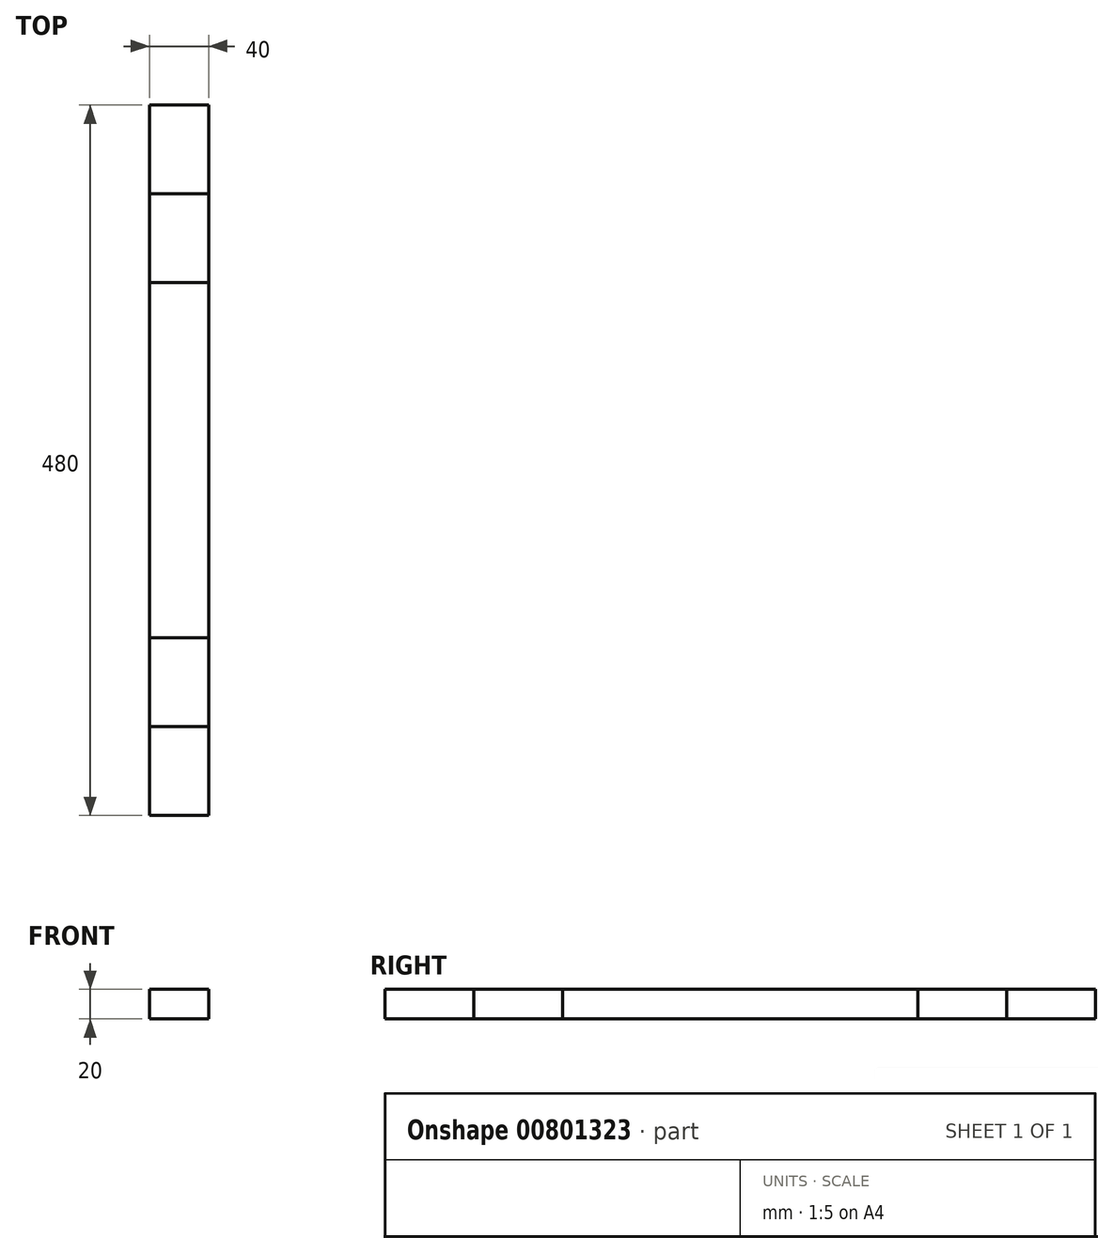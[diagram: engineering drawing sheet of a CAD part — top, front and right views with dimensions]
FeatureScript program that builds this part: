
annotation { "Feature Type Name" : "Feature", "Feature Type Description" : "" }
export const myFeature = defineFeature(function(context is Context, id is Id, definition is map)
    precondition{}
    {
        {
            var Q0;
            Q0=qCreatedBy(makeId("Front.planeOp"),FACE);
            var sketch = newSketch(context, id + "F0", { "sketchPlane" : qUnion([Q0])});
            skLineSegment(sketch, "E0.bottom", {"start": v(20, -10) * mm, "end": v(-20, -10) * mm});
            skLineSegment(sketch, "E0.top", {"start": v(20, 10) * mm, "end": v(-20, 10) * mm});
            skLineSegment(sketch, "E0.left", {"start": v(20, -10) * mm, "end": v(20, 10) * mm});
            skLineSegment(sketch, "E0.right", {"start": v(-20, -10) * mm, "end": v(-20, 10) * mm});
            skPoint(sketch, "E0.middle", {"position": v(0, 0) * mm});
            skSolve(sketch);
        }
        {
            var Q0;
            Q0 = qSketchRegion(id + "F0", true);
            extrude(context, id + "F1", {"entities" : qUnion([Q0]), "endBound" : BoundingType.SYMMETRIC, "depth" : 480 * mm, "offsetDistance" : 25 * mm});
        }
        {
            var Q0;
            Q0=qCreatedBy(makeId("Front.planeOp"),FACE);
            var sketch = newSketch(context, id + "F2", { "sketchPlane" : qUnion([Q0])});
            skLineSegment(sketch, "E1.bottom", {"start": v(20, -10) * mm, "end": v(-20, -10) * mm});
            skLineSegment(sketch, "E1.top", {"start": v(20, 10) * mm, "end": v(-20, 10) * mm});
            skLineSegment(sketch, "E1.left", {"start": v(20, -10) * mm, "end": v(20, 10) * mm});
            skLineSegment(sketch, "E1.right", {"start": v(-20, -10) * mm, "end": v(-20, 10) * mm});
            skPoint(sketch, "E1.middle", {"position": v(0, 0) * mm});
            skSolve(sketch);
        }
        {
            var Q0;
            Q0 = qSketchRegion(id + "F2", true);
            extrude(context, id + "F3", {"entities" : qUnion([Q0]), "endBound" : BoundingType.SYMMETRIC, "depth" : 360 * mm, "offsetDistance" : 25 * mm});
        }
        {
            var Q0;
            Q0=qCreatedBy(makeId("Front.planeOp"),FACE);
            var sketch = newSketch(context, id + "F4", { "sketchPlane" : qUnion([Q0])});
            skLineSegment(sketch, "E2.bottom", {"start": v(20, -10) * mm, "end": v(-20, -10) * mm});
            skLineSegment(sketch, "E2.top", {"start": v(20, 10) * mm, "end": v(-20, 10) * mm});
            skLineSegment(sketch, "E2.left", {"start": v(20, -10) * mm, "end": v(20, 10) * mm});
            skLineSegment(sketch, "E2.right", {"start": v(-20, -10) * mm, "end": v(-20, 10) * mm});
            skPoint(sketch, "E2.middle", {"position": v(0, 0) * mm});
            skSolve(sketch);
        }
        {
            var Q0;
            Q0 = qSketchRegion(id + "F4", true);
            extrude(context, id + "F5", {"entities" : qUnion([Q0]), "endBound" : BoundingType.SYMMETRIC, "depth" : 240 * mm, "offsetDistance" : 25 * mm});
        }
    });
